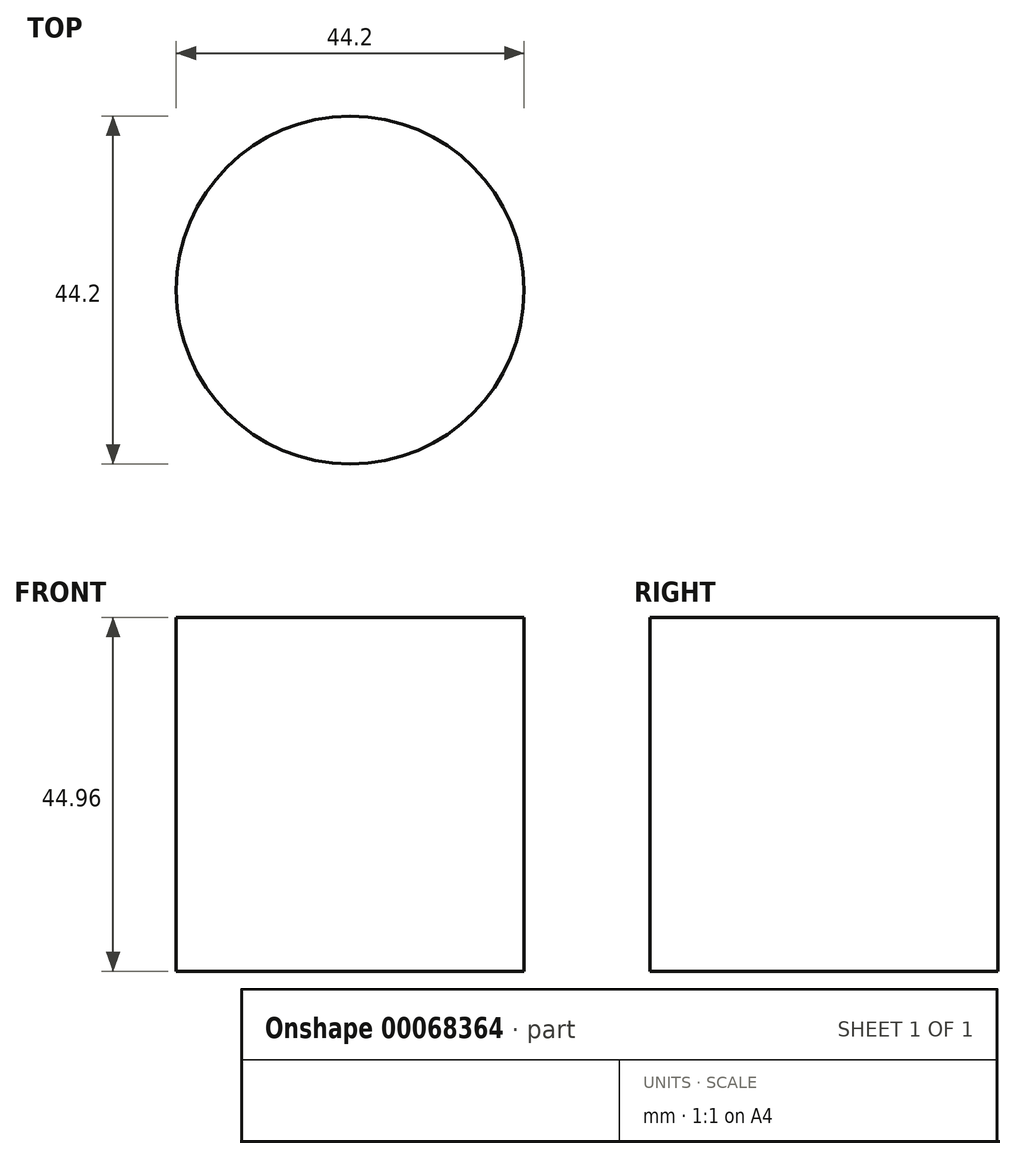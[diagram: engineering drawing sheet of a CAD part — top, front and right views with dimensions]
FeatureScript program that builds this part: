
annotation { "Feature Type Name" : "Feature", "Feature Type Description" : "" }
export const myFeature = defineFeature(function(context is Context, id is Id, definition is map)
    precondition{}
    {
        {
            var Q0;
            Q0=qCreatedBy(makeId("Top.planeOp"),FACE);
            var sketch = newSketch(context, id + "F0", { "sketchPlane" : qUnion([Q0])});
            skCircle(sketch, "E0", {"center": v(0, 0) * mm, "radius": 22.1 * mm});
            skSolve(sketch);
        }
        {
            var Q0;
            Q0 = qSketchRegion(id + "F0", true);
            extrude(context, id + "F1", {"entities" : qUnion([Q0]), "depth" : 44.96 * mm});
        }
    });
